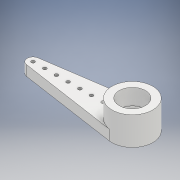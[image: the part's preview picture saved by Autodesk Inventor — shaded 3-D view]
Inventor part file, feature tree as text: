
AUTODESK INVENTOR PART (.ipt)
format: ipt  version: 2018 (Build 220112000, 112)  size: 144,896 bytes
history: native  units: mm
features: sketch x1, other x1
ambient origin geometry x8: Origin, YZ Plane, XZ Plane, XY Plane, X Axis, Y Axis, Z Axis, Center Point
bodies: Solid1 (feature_tree)
feature tree (2):
  sketch  "Sketch1"
  other  "Estrusione-Estrusione2"
